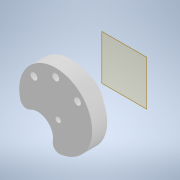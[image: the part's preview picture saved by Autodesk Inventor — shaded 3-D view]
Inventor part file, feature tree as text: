
AUTODESK INVENTOR PART (.ipt)
format: ipt  version: 2022 (Build 260153000, 153)  size: 245,760 bytes
history: native  units: mm
features: extrude x8, sketch x8, other x7, reference x4, fillet x2, projected_geometry x2, chamfer x1, mirror x1
ambient origin geometry x8: Origin, YZ Plane, XZ Plane, XY Plane, X Axis, Y Axis, Z Axis, Center Point
bodies: Body1 (feature_tree)
feature tree (33):
  other  "Твердое тело1"
  other  "РабПлоскость1"
  extrude  "Выдавливание1"  Depth=45.0mm
  extrude  "Выдавливание2"  Depth=10.0mm TaperAngle=0.0deg
  fillet  "Сопряжение1"  Radius=13.0mm
  extrude  "Выдавливание3"  Depth=3.0mm
  extrude  "Выдавливание4"  Depth=10.0mm TaperAngle=0.0deg
  fillet  "Сопряжение2"  Radius=4.0mm
  chamfer  "Фаска1"  Distance=25.2mm
  extrude  "Выдавливание5"  Depth=4.0mm
  extrude  "Выдавливание6"  Depth=0.5mm
  extrude  "Выдавливание7"  Depth=7.8mm TaperAngle=0.0deg
  other  "РабПлоскость2"
  mirror  "Зеркальное отражение1"
  extrude  "Выдавливание8"  Depth=2.0mm
  sketch  "Эскиз1"
  sketch  "Эскиз2"
  reference  "Ссылка1"
  sketch  "Эскиз3"
  sketch  "Эскиз4"
  projected_geometry  "Спроецированная петля1"
  projected_geometry  "Спроецированная петля2"
  sketch  "Эскиз5"
  reference  "Ссылка2"
  sketch  "Эскиз6"
  reference  "Ссылка3"
  sketch  "Эскиз7"
  reference  "Ссылка4"
  sketch  "Эскиз8"
  other  "<userpath>\Documents\Git\MZCAT_2024\MZCAT.iam"
  other  "MZCAT.iam"
  other  "motor:2"
  other  "base plate:2"
